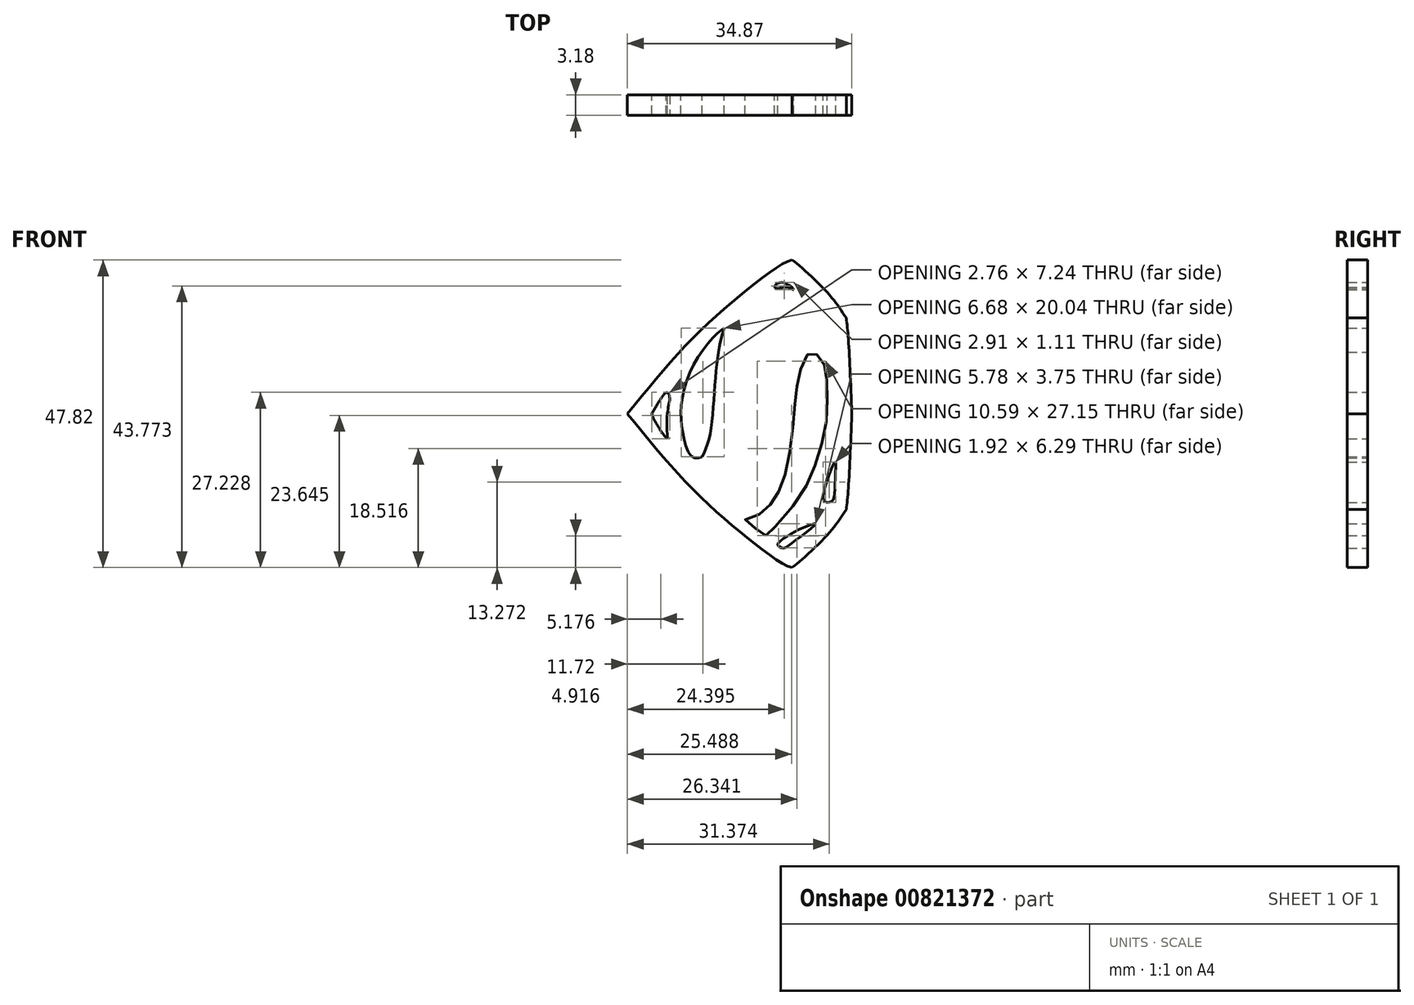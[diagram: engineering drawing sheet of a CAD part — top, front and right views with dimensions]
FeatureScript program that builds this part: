
annotation { "Feature Type Name" : "Feature", "Feature Type Description" : "" }
export const myFeature = defineFeature(function(context is Context, id is Id, definition is map)
    precondition{}
    {
        {
            var Q0;
            Q0=qCreatedBy(makeId("Front.planeOp"),FACE);
            var sketch = newSketch(context, id + "F0", { "sketchPlane" : qUnion([Q0])});
            skFitSpline(sketch, "E0", {"points": [v(-21.04, 47.36) * mm, v(-15.81, 47.36) * mm, v(-10, 46.63) * mm, v(-3.76, 44.6) * mm, v(2.62, 41.99) * mm, v(9.74, 38.21) * mm, v(17, 32.55) * mm, v(24.11, 26.02) * mm, v(30.94, 17.6) * mm, v(31.16, 17.07) * mm], "startDerivative": vector(51.79, 1.09) * mm, "endDerivative": vector(2.7, -11.12) * mm});
            skFitSpline(sketch, "E1", {"points": [v(31.16, 17.07) * mm, v(25.32, 17.07) * mm, v(22.64, 16.61) * mm, v(20.77, 15.58) * mm, v(20.1, 14.46) * mm, v(19.73, 5.26) * mm], "startDerivative": vector(-27.8, 0.53) * mm, "endDerivative": vector(0.96, -37) * mm});
            skFitSpline(sketch, "E2", {"points": [v(19.73, 5.26) * mm, v(21.56, 5.26) * mm, v(23.1, 4.99) * mm, v(24.98, 3.72) * mm, v(26.22, 2.7) * mm], "startDerivative": vector(6.72, 0.3) * mm, "endDerivative": vector(4.9, -4.18) * mm});
            skFitSpline(sketch, "E3", {"points": [v(26.22, 2.7) * mm, v(23.7, 1.87) * mm, v(22.05, 0.91) * mm, v(20.6, -0.56) * mm, v(20.25, -2.63) * mm], "startDerivative": vector(-7.25, -1.04) * mm, "endDerivative": vector(-0.08, -9.17) * mm});
            skFitSpline(sketch, "E4", {"points": [v(-21.04, 47.36) * mm, v(-14.63, 43.04) * mm, v(-11.06, 40.04) * mm, v(-9.8, 34.63) * mm, v(-13.25, 30.13) * mm, v(-15.32, 29) * mm], "startDerivative": vector(16.64, -13.44) * mm, "endDerivative": vector(-14.87, -5.9) * mm});
            skFitSpline(sketch, "E5", {"points": [v(-15.32, 29) * mm, v(-13.1, 28.23) * mm, v(-8.17, 25.51) * mm, v(-5.07, 19.4) * mm, v(-5.07, 19.4) * mm, v(-13.75, 4.72) * mm, v(-18.55, -0.52) * mm, v(-20.68, -2.63) * mm], "startDerivative": vector(23.87, -9.84) * mm, "endDerivative": vector(-19.45, -17.88) * mm});
            skLineSegment(sketch, "E6", {"start": v(-24.65, -2.63) * mm, "end": v(30.72, -2.63) * mm, "construction": true});
            skFitSpline(sketch, "E7.MirrorCS", {"points": [v(26.22, -7.95) * mm, v(23.7, -7.13) * mm, v(22.05, -6.17) * mm, v(20.6, -4.7) * mm, v(20.25, -2.63) * mm], "startDerivative": vector(-7.25, 1.04) * mm, "endDerivative": vector(-0.08, 9.17) * mm});
            skFitSpline(sketch, "E8.MirrorCS", {"points": [v(19.73, -10.52) * mm, v(21.56, -10.52) * mm, v(23.1, -10.24) * mm, v(24.98, -8.98) * mm, v(26.22, -7.95) * mm], "startDerivative": vector(6.72, -0.3) * mm, "endDerivative": vector(4.9, 4.18) * mm});
            skFitSpline(sketch, "E9.MirrorCS", {"points": [v(31.16, -22.33) * mm, v(25.32, -22.33) * mm, v(22.64, -21.87) * mm, v(20.77, -20.84) * mm, v(20.1, -19.72) * mm, v(19.73, -10.52) * mm], "startDerivative": vector(-27.8, -0.53) * mm, "endDerivative": vector(0.96, 37) * mm});
            skFitSpline(sketch, "E10.MirrorCS", {"points": [v(-21.04, -52.62) * mm, v(-15.81, -52.62) * mm, v(-10, -51.9) * mm, v(-3.76, -49.86) * mm, v(2.62, -47.25) * mm, v(9.74, -43.47) * mm, v(17, -37.8) * mm, v(24.11, -31.28) * mm, v(30.94, -22.86) * mm, v(31.16, -22.33) * mm], "startDerivative": vector(51.79, -1.09) * mm, "endDerivative": vector(2.7, 11.12) * mm});
            skFitSpline(sketch, "E11.MirrorCS", {"points": [v(-21.04, -52.62) * mm, v(-14.63, -48.3) * mm, v(-11.06, -45.3) * mm, v(-9.8, -39.88) * mm, v(-13.25, -35.4) * mm, v(-15.32, -34.26) * mm], "startDerivative": vector(16.64, 13.44) * mm, "endDerivative": vector(-14.87, 5.9) * mm});
            skFitSpline(sketch, "E12.MirrorCS", {"points": [v(-15.32, -34.26) * mm, v(-13.1, -33.48) * mm, v(-8.17, -30.77) * mm, v(-5.07, -24.67) * mm, v(-5.07, -24.67) * mm, v(-13.75, -9.98) * mm, v(-18.55, -4.74) * mm, v(-20.68, -2.63) * mm], "startDerivative": vector(23.87, 9.84) * mm, "endDerivative": vector(-19.45, 17.88) * mm});
            skLineSegment(sketch, "E13", {"start": v(6.56, -31.69) * mm, "end": v(6.56, 31.69) * mm, "construction": true});
            skFitSpline(sketch, "E14", {"points": [v(16.65, -2.63) * mm, v(16.1, 8.82) * mm, v(15.77, 12.27) * mm], "startDerivative": vector(-0.8, 20.33) * mm, "endDerivative": vector(-0.95, 8.3) * mm});
            skFitSpline(sketch, "E15", {"points": [v(15.77, 12.27) * mm, v(12.46, 16.64) * mm, v(7.36, 21.28) * mm], "startDerivative": vector(-6.4, 9.4) * mm, "endDerivative": vector(-3.05, 1.66) * mm});
            skFitSpline(sketch, "E16", {"points": [v(7.36, 21.28) * mm, v(1.73, 17.72) * mm, v(-8.1, 9.1) * mm, v(-18.22, -2.63) * mm], "startDerivative": vector(-13.82, -2.57) * mm, "endDerivative": vector(-25.21, -31.02) * mm});
            skFitSpline(sketch, "E17", {"points": [v(-11.99, -6.51) * mm, v(-12.03, -2.63) * mm, v(-11.66, -0.33) * mm, v(-12.2, 0.72) * mm], "startDerivative": vector(-0.69, 9.3) * mm, "endDerivative": vector(-5.98, 2.33) * mm});
            skFitSpline(sketch, "E18", {"points": [v(-12.2, 0.72) * mm, v(-13.35, -0.8) * mm, v(-14.42, -2.63) * mm], "startDerivative": vector(-3.02, -2.78) * mm, "endDerivative": vector(-1.95, -3.79) * mm});
            skFitSpline(sketch, "E19", {"points": [v(-14.42, -2.63) * mm, v(-13.65, -4.28) * mm, v(-12.86, -5.55) * mm, v(-11.99, -6.51) * mm], "startDerivative": vector(0.56, -4.35) * mm, "endDerivative": vector(2.23, -1.28) * mm});
            skFitSpline(sketch, "E20.MirrorCS", {"points": [v(16.65, -2.63) * mm, v(16.1, -14.08) * mm, v(15.77, -17.53) * mm], "startDerivative": vector(-0.8, -20.33) * mm, "endDerivative": vector(-0.95, -8.3) * mm});
            skFitSpline(sketch, "E21.MirrorCS", {"points": [v(15.77, -17.53) * mm, v(12.46, -21.9) * mm, v(7.36, -26.54) * mm], "startDerivative": vector(-6.4, -9.4) * mm, "endDerivative": vector(-3.05, -1.66) * mm});
            skFitSpline(sketch, "E22.MirrorCS", {"points": [v(7.36, -26.54) * mm, v(1.73, -22.98) * mm, v(-8.1, -14.35) * mm, v(-18.22, -2.63) * mm], "startDerivative": vector(-13.82, 2.57) * mm, "endDerivative": vector(-25.21, 31.02) * mm});
            skFitSpline(sketch, "E23", {"points": [v(-3.16, 10.7) * mm, v(-3.83, 8.37) * mm, v(-4.58, 2.44) * mm, v(-5.35, -5.65) * mm, v(-6.62, -9.33) * mm], "startDerivative": vector(-3.91, -11.71) * mm, "endDerivative": vector(-7.77, -13.72) * mm});
            skFitSpline(sketch, "E24", {"points": [v(-6.62, -9.33) * mm, v(-7.48, -9.52) * mm, v(-8.38, -9.13) * mm, v(-9.32, -6.97) * mm, v(-9.82, -4.19) * mm, v(-9.82, -1.03) * mm, v(-8.7, 3.39) * mm, v(-6.24, 7.63) * mm, v(-4.08, 10.01) * mm, v(-3.16, 10.7) * mm], "startDerivative": vector(-12.82, -4.34) * mm, "endDerivative": vector(11.18, 7.53) * mm});
            skFitSpline(sketch, "E25", {"points": [v(7.63, 16.68) * mm, v(6.56, 17.03) * mm, v(5.3, 16.86) * mm, v(4.65, 17.04) * mm, v(5.7, 17.8) * mm, v(7.63, 16.68) * mm]});
            skFitSpline(sketch, "E26", {"points": [v(14.06, -10.12) * mm, v(14.02, -13.31) * mm, v(13.77, -15.93) * mm, v(13.09, -16.4) * mm, v(12.3, -16.14) * mm, v(12.78, -13.09) * mm, v(14.06, -10.12) * mm]});
            skFitSpline(sketch, "E27", {"points": [v(11.01, -19.75) * mm, v(8.25, -22.06) * mm, v(6.22, -23.48) * mm, v(5.58, -23.43) * mm, v(5.13, -23) * mm, v(6.05, -22.03) * mm, v(8.87, -20.44) * mm, v(11.01, -19.75) * mm]});
            skFitSpline(sketch, "E28", {"points": [v(3.29, -21.6) * mm, v(2.34, -20.86) * mm, v(0.03, -19.23) * mm, v(1.45, -18.6) * mm, v(3.44, -17.34) * mm, v(4.81, -15.55) * mm, v(6.1, -12.66) * mm, v(7.18, -7.45) * mm, v(7.78, -1.21) * mm, v(8.2, 2.07) * mm, v(9.02, 5.18) * mm, v(10.2, 6.94) * mm, v(11.26, 6.54) * mm, v(12.26, 5.23) * mm, v(12.7, 2.97) * mm, v(12.83, -1.1) * mm, v(12.33, -5.9) * mm, v(10.65, -11.34) * mm, v(8.2, -16.05) * mm, v(3.94, -21.07) * mm, v(3.29, -21.6) * mm]});
            skLineSegment(sketch, "E29", {"start": v(-57.93, -81.37) * mm, "end": v(-57.93, 55.63) * mm, "construction": true});
            skLineSegment(sketch, "E30", {"start": v(-57.93, 55.63) * mm, "end": v(-19.93, 55.63) * mm, "construction": true});
            skLineSegment(sketch, "E31", {"start": v(-19.93, 55.63) * mm, "end": v(-19.93, 35.63) * mm, "construction": true});
            skArc(sketch, "E32", {"start": v(-5.07, 19.4) * mm, "mid": v(-6.58, 32.54) * mm, "end": v(-14.63, 43.04) * mm});
            skArc(sketch, "E33", {"start": v(-14.63, -48.3) * mm, "mid": v(-6.58, -37.8) * mm, "end": v(-5.07, -24.67) * mm});
            skSolve(sketch);
        }
        {
            var Q0;
            Q0=makeQuery(id+"F0.imprint","IMPRINT",FACE,{"disambiguationData":[TD([[makeQuery(id+"F0.imprint","IMPRINT",EDGE,{"derivedFrom":sQuery(id+"F0.wireOp",EDGE,"E14")}),1.0]])]});
            var Q1;
            Q1=makeQuery(id+"F0.imprint","IMPRINT",FACE,{"disambiguationData":[TD([[makeQuery(id+"F0.imprint","IMPRINT",EDGE,{"derivedFrom":sQuery(id+"F0.wireOp",EDGE,"E0")}),-1.0]])]});
            extrude(context, id + "F1", {"entities" : qUnion([Q0, Q1]), "depth" : 3.17 * mm, "offsetDistance" : 25.4 * mm});
        }
    });
